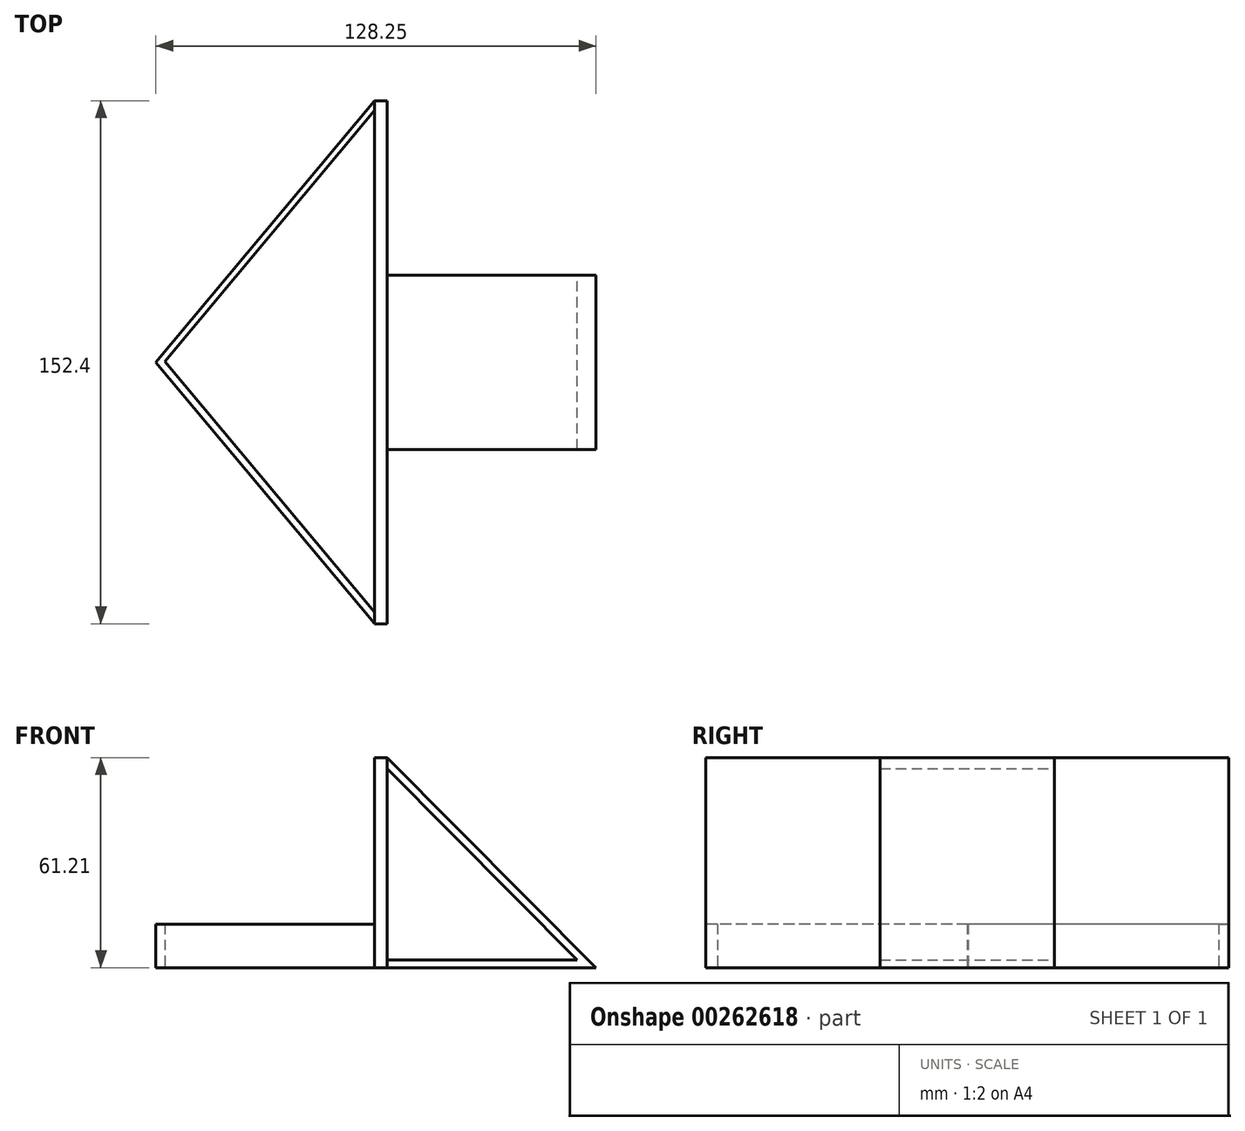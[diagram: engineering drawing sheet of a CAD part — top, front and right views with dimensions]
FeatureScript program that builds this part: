
annotation { "Feature Type Name" : "Feature", "Feature Type Description" : "" }
export const myFeature = defineFeature(function(context is Context, id is Id, definition is map)
    precondition{}
    {
        {
            var Q0;
            Q0=qCreatedBy(makeId("Front.planeOp"),FACE);
            var sketch = newSketch(context, id + "F0", { "sketchPlane" : qUnion([Q0])});
            skLineSegment(sketch, "E0", {"start": v(0, 0) * mm, "end": v(0, 61.21) * mm});
            skLineSegment(sketch, "E1", {"start": v(0, 61.21) * mm, "end": v(3.57, 61.21) * mm});
            skLineSegment(sketch, "E2", {"start": v(3.57, 61.21) * mm, "end": v(3.57, 0) * mm});
            skLineSegment(sketch, "E3", {"start": v(3.57, 0) * mm, "end": v(0, 0) * mm});
            skLineSegment(sketch, "E4", {"start": v(3.57, 61.21) * mm, "end": v(64.48, 0) * mm});
            skLineSegment(sketch, "E5", {"start": v(64.48, 0) * mm, "end": v(3.57, 0) * mm});
            skLineSegment(sketch, "E6", {"start": v(3.57, 57.97) * mm, "end": v(58.98, 2.29) * mm});
            skLineSegment(sketch, "E7", {"start": v(58.98, 2.29) * mm, "end": v(3.57, 2.29) * mm});
            skSolve(sketch);
        }
        {
            var Q0;
            Q0=makeQuery(id+"F0.imprint","IMPRINT",FACE,{"disambiguationData":[TD([[makeQuery(id+"F0.imprint","IMPRINT",EDGE,{"derivedFrom":sQuery(id+"F0.wireOp",EDGE,"E0")}),-1.0]])]});
            extrude(context, id + "F1", {"entities" : qUnion([Q0]), "depth" : 101.6 * mm});
        }
        {
            var Q0;
            {var subQ1=sQuery(id+"F0.wireOp",EDGE,"E4");Q0=makeQuery(id+"F0.imprint","IMPRINT",FACE,{"disambiguationData":[TD([[makeQuery(id+"F0.imprint","IMPRINT",EDGE,{"derivedFrom":subQ1}),-1.0]])]});}
            extrude(context, id + "F2", {"entities" : qUnion([Q0]), "operationType" : NewBodyOperationType.ADD, "depth" : 50.8 * mm});
        }
        {
            var Q0;
            Q0=makeQuery(id+"F0.imprint","IMPRINT",FACE,{"disambiguationData":[TD([[makeQuery(id+"F0.imprint","IMPRINT",EDGE,{"derivedFrom":sQuery(id+"F0.wireOp",EDGE,"E0")}),-1.0]])]});
            extrude(context, id + "F3", {"entities" : qUnion([Q0]), "operationType" : NewBodyOperationType.ADD, "oppositeDirection" : true, "depth" : 50.8 * mm});
        }
        {
            var Q0;
            Q0=qCreatedBy(makeId("Top.planeOp"),FACE);
            var sketch = newSketch(context, id + "F4", { "sketchPlane" : qUnion([Q0])});
            skLineSegment(sketch, "E8", {"start": v(0, 50.73) * mm, "end": v(-63.77, -25.4) * mm});
            skLineSegment(sketch, "E9", {"start": v(-63.77, -25.4) * mm, "end": v(0, -101.54) * mm});
            skLineSegment(sketch, "E10", {"start": v(0, 47.9) * mm, "end": v(-61.2, -25.15) * mm});
            skLineSegment(sketch, "E11", {"start": v(-61.2, -25.15) * mm, "end": v(0, -98.2) * mm});
            skLineSegment(sketch, "E12", {"start": v(0, 47.9) * mm, "end": v(0, 50.73) * mm});
            skLineSegment(sketch, "E13", {"start": v(0, -98.2) * mm, "end": v(0, -101.54) * mm});
            skSolve(sketch);
        }
        {
            var Q0;
            Q0=makeQuery(id+"F4.imprint","IMPRINT",FACE,{"disambiguationData":[TD([[makeQuery(id+"F4.imprint","IMPRINT",EDGE,{"derivedFrom":sQuery(id+"F4.wireOp",EDGE,"E8")}),1.0]])]});
            extrude(context, id + "F5", {"entities" : qUnion([Q0]), "operationType" : NewBodyOperationType.ADD, "depth" : 12.7 * mm});
        }
    });
